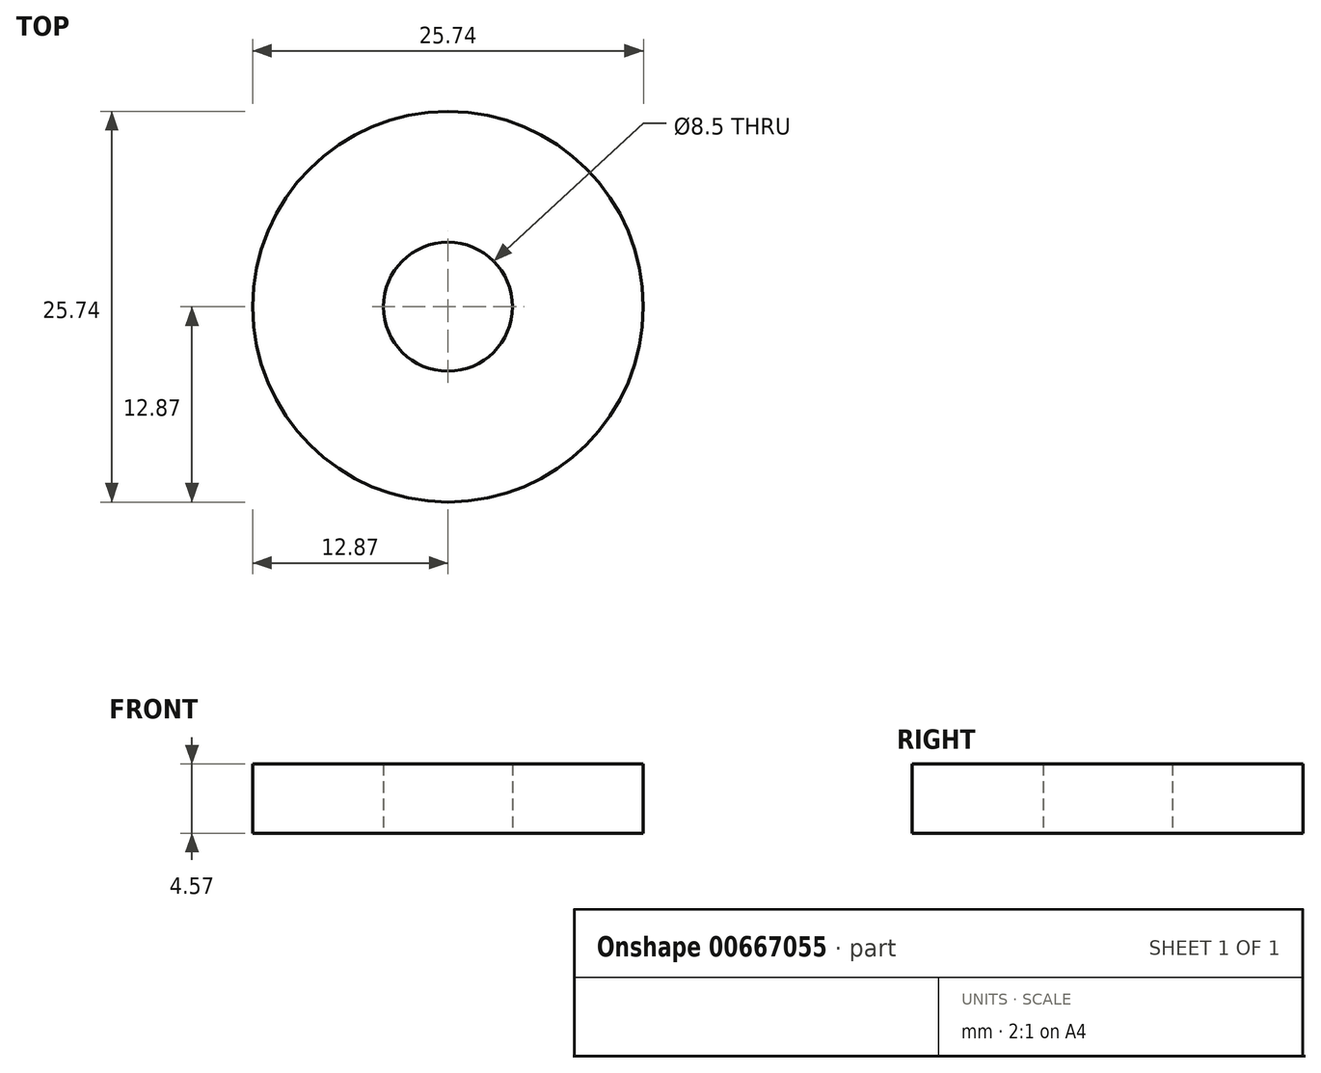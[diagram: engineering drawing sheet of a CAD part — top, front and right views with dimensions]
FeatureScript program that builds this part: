
annotation { "Feature Type Name" : "Feature", "Feature Type Description" : "" }
export const myFeature = defineFeature(function(context is Context, id is Id, definition is map)
    precondition{}
    {
        {
            var Q0;
            Q0=qCreatedBy(makeId("Top.planeOp"),FACE);
            var sketch = newSketch(context, id + "F0", { "sketchPlane" : qUnion([Q0])});
            skCircle(sketch, "E0", {"center": v(0, 0) * mm, "radius": 4.25 * mm});
            skCircle(sketch, "E1", {"center": v(0, 0) * mm, "radius": 12.87 * mm});
            skSolve(sketch);
        }
        {
            var Q0;
            Q0=makeQuery(id+"F0.imprint","IMPRINT",FACE,{"disambiguationData":[TD([[makeQuery(id+"F0.imprint","IMPRINT",EDGE,{"derivedFrom":sQuery(id+"F0.wireOp",EDGE,"E0")}),-1.0]])]});
            extrude(context, id + "F1", {"entities" : qUnion([Q0]), "depth" : 4.57 * mm, "offsetDistance" : 25.4 * mm});
        }
    });
